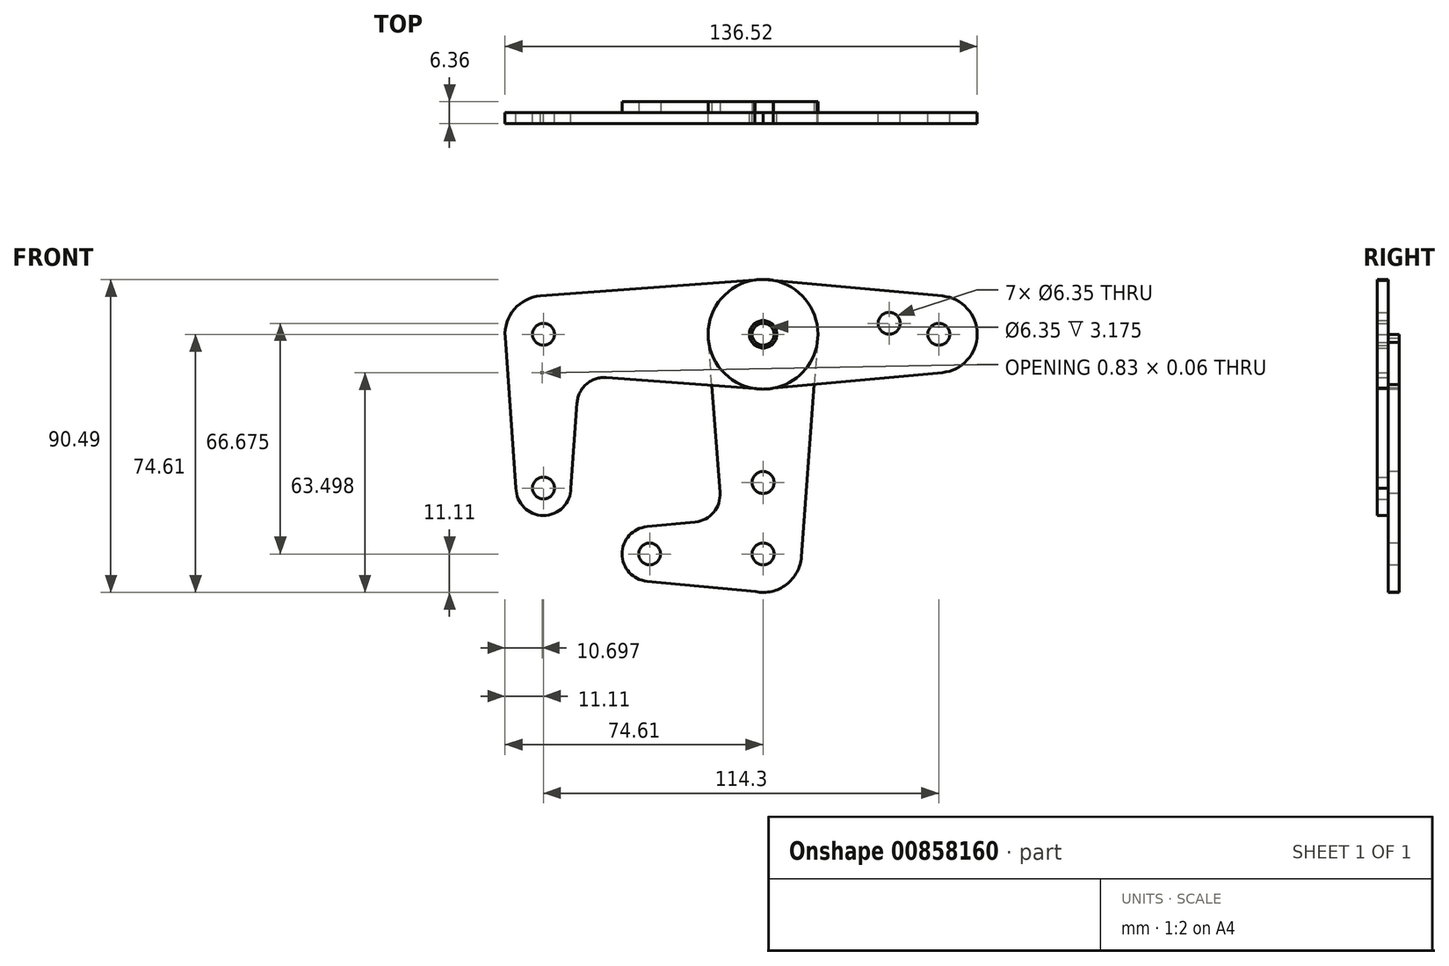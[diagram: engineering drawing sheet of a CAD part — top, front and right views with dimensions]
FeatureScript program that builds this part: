
annotation { "Feature Type Name" : "Feature", "Feature Type Description" : "" }
export const myFeature = defineFeature(function(context is Context, id is Id, definition is map)
    precondition{}
    {
        {
            var Q0;
            Q0=qCreatedBy(makeId("Front.planeOp"),FACE);
            var sketch = newSketch(context, id + "F0", { "sketchPlane" : qUnion([Q0])});
            skCircle(sketch, "E0", {"center": v(0, 0) * mm, "radius": 15.88 * mm});
            skLineSegment(sketch, "E1", {"start": v(3.17, 0) * mm, "end": v(3.98, 0) * mm});
            skLineSegment(sketch, "E2", {"start": v(-3.17, 0) * mm, "end": v(-3.98, 0) * mm});
            skCircle(sketch, "E3", {"center": v(-63.5, 0) * mm, "radius": 11.11 * mm});
            skLineSegment(sketch, "E4", {"start": v(-63.5, -11.11) * mm, "end": v(-63.5, -11.14) * mm});
            skCircle(sketch, "E5", {"center": v(-63.5, -44.45) * mm, "radius": 7.94 * mm});
            skCircle(sketch, "E6", {"center": v(50.8, 0) * mm, "radius": 11.11 * mm});
            skCircle(sketch, "E7", {"center": v(36.46, 3.17) * mm, "radius": 3.17 * mm});
            skCircle(sketch, "E8", {"center": v(-63.5, -44.45) * mm, "radius": 3.18 * mm});
            skCircle(sketch, "E9", {"center": v(-63.5, 0) * mm, "radius": 3.18 * mm});
            skCircle(sketch, "E10", {"center": v(0, 0) * mm, "radius": 3.18 * mm});
            skCircle(sketch, "E11", {"center": v(0, 0) * mm, "radius": 3.98 * mm});
            skCircle(sketch, "E12", {"center": v(50.8, 0) * mm, "radius": 3.18 * mm});
            skLineSegment(sketch, "E13", {"start": v(-55.56, -44.45) * mm, "end": v(-53.8, -19.86) * mm});
            skLineSegment(sketch, "E14", {"start": v(-71.44, -44.45) * mm, "end": v(-74.58, -0.8) * mm});
            skLineSegment(sketch, "E15", {"start": v(0, -15.88) * mm, "end": v(-45.27, -12.5) * mm});
            skLineSegment(sketch, "E16", {"start": v(0, 15.88) * mm, "end": v(-64.33, 11.08) * mm});
            skLineSegment(sketch, "E17", {"start": v(0, -15.88) * mm, "end": v(51.83, -11.06) * mm});
            skLineSegment(sketch, "E18", {"start": v(0, 15.88) * mm, "end": v(51.83, 11.06) * mm});
            skLineSegment(sketch, "E19.trimOffspring", {"start": v(-63.5, -11.14) * mm, "end": v(-64.33, -11.08) * mm});
            skPoint(sketch, "E20.visualSharp", {"position": v(-53.22, -11.9) * mm});
            skArc(sketch, "E20.filletArc", {"start": v(-45.27, -12.5) * mm, "mid": v(-51.06, -14.41) * mm, "end": v(-53.8, -19.86) * mm});
            skArc(sketch, "E21", {"start": v(-2.1, -74.41) * mm, "mid": v(6.75, -72.33) * mm, "end": v(11.08, -64.33) * mm});
            skLineSegment(sketch, "E22", {"start": v(15.88, 0) * mm, "end": v(11.08, -64.33) * mm});
            skCircle(sketch, "E23", {"center": v(-32.8, -63.5) * mm, "radius": 7.94 * mm});
            skLineSegment(sketch, "E24", {"start": v(-12.46, -45.75) * mm, "end": v(-15.83, -1.2) * mm});
            skLineSegment(sketch, "E25", {"start": v(-2.1, -74.41) * mm, "end": v(-33.56, -71.4) * mm});
            skLineSegment(sketch, "E26.trimOffspring", {"start": v(-19.63, -54.27) * mm, "end": v(-33.56, -55.6) * mm});
            skPoint(sketch, "E27.start.orphan", {"position": v(0, -52.39) * mm});
            skPoint(sketch, "E28.orphan", {"position": v(0, -74.61) * mm});
            skPoint(sketch, "E29.visualSharp", {"position": v(-11.87, -53.52) * mm});
            skArc(sketch, "E29.filletArc", {"start": v(-19.63, -54.27) * mm, "mid": v(-14.3, -51.47) * mm, "end": v(-12.46, -45.75) * mm});
            skCircle(sketch, "E30", {"center": v(-32.8, -63.5) * mm, "radius": 3.18 * mm});
            skCircle(sketch, "E31", {"center": v(0, -63.5) * mm, "radius": 3.18 * mm});
            skCircle(sketch, "E32", {"center": v(0, -42.85) * mm, "radius": 3.18 * mm});
            skLineSegment(sketch, "E33.trimOffspring", {"start": v(-60.32, 0) * mm, "end": v(-63.5, 0) * mm});
            skSolve(sketch);
        }
        {
            var Q0;
            {var subQ0=sQuery(id+"F0.wireOp",EDGE,"E18");var subQ1=sQuery(id+"F0.wireOp",EDGE,"E0");var subQ3=makeQuery(id+"F0.imprint","INTERSECT",VERTEX,{"derivedFrom":[subQ1,subQ0]});Q0=makeQuery(id+"F0.imprint","IMPRINT",FACE,{"disambiguationData":[TD([[makeQuery(id+"F0.imprint","IMPRINT",EDGE,{"disambiguationData":[TD([[subQ3,-1.0]])],"derivedFrom":subQ1}),1.0]])]});}
            var Q1;
            {var subQ0=sQuery(id+"F0.wireOp",EDGE,"E16");var subQ1=sQuery(id+"F0.wireOp",EDGE,"E0");var subQ3=makeQuery(id+"F0.imprint","INTERSECT",VERTEX,{"derivedFrom":[subQ1,subQ0]});Q1=makeQuery(id+"F0.imprint","IMPRINT",FACE,{"disambiguationData":[TD([[makeQuery(id+"F0.imprint","IMPRINT",EDGE,{"disambiguationData":[TD([[subQ3,1.0]])],"derivedFrom":subQ1}),1.0]])]});}
            var Q2;
            Q2=makeQuery(id+"F0.imprint","IMPRINT",FACE,{"disambiguationData":[TD([[makeQuery(id+"F0.imprint","IMPRINT",EDGE,{"derivedFrom":sQuery(id+"F0.wireOp",EDGE,"E8")}),-1.0]])]});
            var Q3;
            Q3=makeQuery(id+"F0.imprint","IMPRINT",FACE,{"disambiguationData":[TD([[makeQuery(id+"F0.imprint","IMPRINT",EDGE,{"derivedFrom":sQuery(id+"F0.wireOp",EDGE,"E12")}),-1.0]])]});
            var Q4;
            {var subQ0=sQuery(id+"F0.wireOp",EDGE,"E24");var subQ1=sQuery(id+"F0.wireOp",EDGE,"E0");var subQ2=makeQuery(id+"F0.imprint","INTERSECT",VERTEX,{"derivedFrom":[subQ1,subQ0]});Q4=makeQuery(id+"F0.imprint","IMPRINT",FACE,{"disambiguationData":[TD([[makeQuery(id+"F0.imprint","IMPRINT",EDGE,{"disambiguationData":[TD([[subQ2,-1.0]])],"derivedFrom":subQ1}),-1.0]])]});}
            var Q5;
            {var subQ0=sQuery(id+"F0.wireOp",EDGE,"E17");var subQ1=sQuery(id+"F0.wireOp",EDGE,"E0");var subQ2=makeQuery(id+"F0.imprint","INTERSECT",VERTEX,{"derivedFrom":[subQ1,subQ0]});Q5=makeQuery(id+"F0.imprint","IMPRINT",FACE,{"disambiguationData":[TD([[makeQuery(id+"F0.imprint","IMPRINT",EDGE,{"disambiguationData":[TD([[subQ2,-1.0]])],"derivedFrom":subQ1}),-1.0]])]});}
            var Q6;
            Q6=makeQuery(id+"F0.imprint","IMPRINT",FACE,{"disambiguationData":[TD([[makeQuery(id+"F0.imprint","IMPRINT",EDGE,{"derivedFrom":sQuery(id+"F0.wireOp",EDGE,"E9")}),-1.0]])]});
            var Q7;
            Q7=makeQuery(id+"F0.imprint","IMPRINT",FACE,{"disambiguationData":[TD([[makeQuery(id+"F0.imprint","IMPRINT",EDGE,{"derivedFrom":sQuery(id+"F0.wireOp",EDGE,"E7")}),-1.0]])]});
            var Q8;
            {var subQ14=sQuery(id+"F0.wireOp",EDGE,"E4");Q8=makeQuery(id+"F0.imprint","IMPRINT",FACE,{"disambiguationData":[TD([[makeQuery(id+"F0.imprint","IMPRINT",EDGE,{"derivedFrom":subQ14}),1.0]])]});}
            var Q9;
            {var subQ2=sQuery(id+"F0.wireOp",EDGE,"E0");var subQ10=sQuery(id+"F0.wireOp",EDGE,"E22");var subQ13=makeQuery(id+"F0.imprint","INTERSECT",VERTEX,{"disambiguationData":[OD(0.0)],"derivedFrom":[subQ2,subQ10]});Q9=makeQuery(id+"F0.imprint","IMPRINT",FACE,{"disambiguationData":[TD([[makeQuery(id+"F0.imprint","IMPRINT",EDGE,{"disambiguationData":[TD([[subQ13,-1.0]])],"derivedFrom":subQ2}),1.0]])]});}
            var Q10;
            {var subQ0=sQuery(id+"F0.wireOp",EDGE,"E1");Q10=makeQuery(id+"F0.imprint","IMPRINT",FACE,{"disambiguationData":[TD([[makeQuery(id+"F0.imprint","IMPRINT",EDGE,{"derivedFrom":subQ0}),-1.0]])]});}
            var Q11;
            {var subQ0=sQuery(id+"F0.wireOp",EDGE,"E1");Q11=makeQuery(id+"F0.imprint","IMPRINT",FACE,{"disambiguationData":[TD([[makeQuery(id+"F0.imprint","IMPRINT",EDGE,{"derivedFrom":subQ0}),1.0]])]});}
            extrude(context, id + "F1", {"entities" : qUnion([Q0, Q1, Q2, Q3, Q4, Q5, Q6, Q7, Q8, Q9, Q10, Q11]), "depth" : 3.17 * mm, "offsetDistance" : 25.4 * mm});
        }
        {
            var Q0;
            {var subQ6=sQuery(id+"F0.wireOp",EDGE,"E25");Q0=makeQuery(id+"F0.imprint","IMPRINT",FACE,{"disambiguationData":[TD([[makeQuery(id+"F0.imprint","IMPRINT",EDGE,{"derivedFrom":subQ6}),-1.0]])]});}
            var Q1;
            Q1=makeQuery(id+"F0.imprint","IMPRINT",FACE,{"disambiguationData":[TD([[makeQuery(id+"F0.imprint","IMPRINT",EDGE,{"derivedFrom":sQuery(id+"F0.wireOp",EDGE,"E31")}),-1.0]])]});
            var Q2;
            Q2=makeQuery(id+"F0.imprint","IMPRINT",FACE,{"disambiguationData":[TD([[makeQuery(id+"F0.imprint","IMPRINT",EDGE,{"derivedFrom":sQuery(id+"F0.wireOp",EDGE,"E30")}),-1.0]])]});
            var Q3;
            {var subQ2=sQuery(id+"F0.wireOp",EDGE,"E0");var subQ10=sQuery(id+"F0.wireOp",EDGE,"E22");var subQ13=makeQuery(id+"F0.imprint","INTERSECT",VERTEX,{"disambiguationData":[OD(0.0)],"derivedFrom":[subQ2,subQ10]});Q3=makeQuery(id+"F0.imprint","IMPRINT",FACE,{"disambiguationData":[TD([[makeQuery(id+"F0.imprint","IMPRINT",EDGE,{"disambiguationData":[TD([[subQ13,-1.0]])],"derivedFrom":subQ2}),1.0]])]});}
            extrude(context, id + "F2", {"entities" : qUnion([Q0, Q1, Q2, Q3]), "operationType" : NewBodyOperationType.ADD, "oppositeDirection" : true, "depth" : 3.17 * mm, "offsetDistance" : 25.4 * mm});
        }
        {
            var Q0;
            {var subQ0=sQuery(id+"F0.wireOp",EDGE,"E17");var subQ1=sQuery(id+"F0.wireOp",EDGE,"E0");var subQ2=makeQuery(id+"F0.imprint","INTERSECT",VERTEX,{"derivedFrom":[subQ1,subQ0]});Q0=makeQuery(id+"F0.imprint","IMPRINT",FACE,{"disambiguationData":[TD([[makeQuery(id+"F0.imprint","IMPRINT",EDGE,{"disambiguationData":[TD([[subQ2,-1.0]])],"derivedFrom":subQ1}),-1.0]])]});}
            var Q1;
            {var subQ0=sQuery(id+"F0.wireOp",EDGE,"E24");var subQ1=sQuery(id+"F0.wireOp",EDGE,"E0");var subQ2=makeQuery(id+"F0.imprint","INTERSECT",VERTEX,{"derivedFrom":[subQ1,subQ0]});Q1=makeQuery(id+"F0.imprint","IMPRINT",FACE,{"disambiguationData":[TD([[makeQuery(id+"F0.imprint","IMPRINT",EDGE,{"disambiguationData":[TD([[subQ2,-1.0]])],"derivedFrom":subQ1}),-1.0]])]});}
            extrude(context, id + "F3", {"entities" : qUnion([Q0, Q1]), "oppositeDirection" : true, "depth" : 3.17 * mm, "offsetDistance" : 25.4 * mm});
        }
    });
